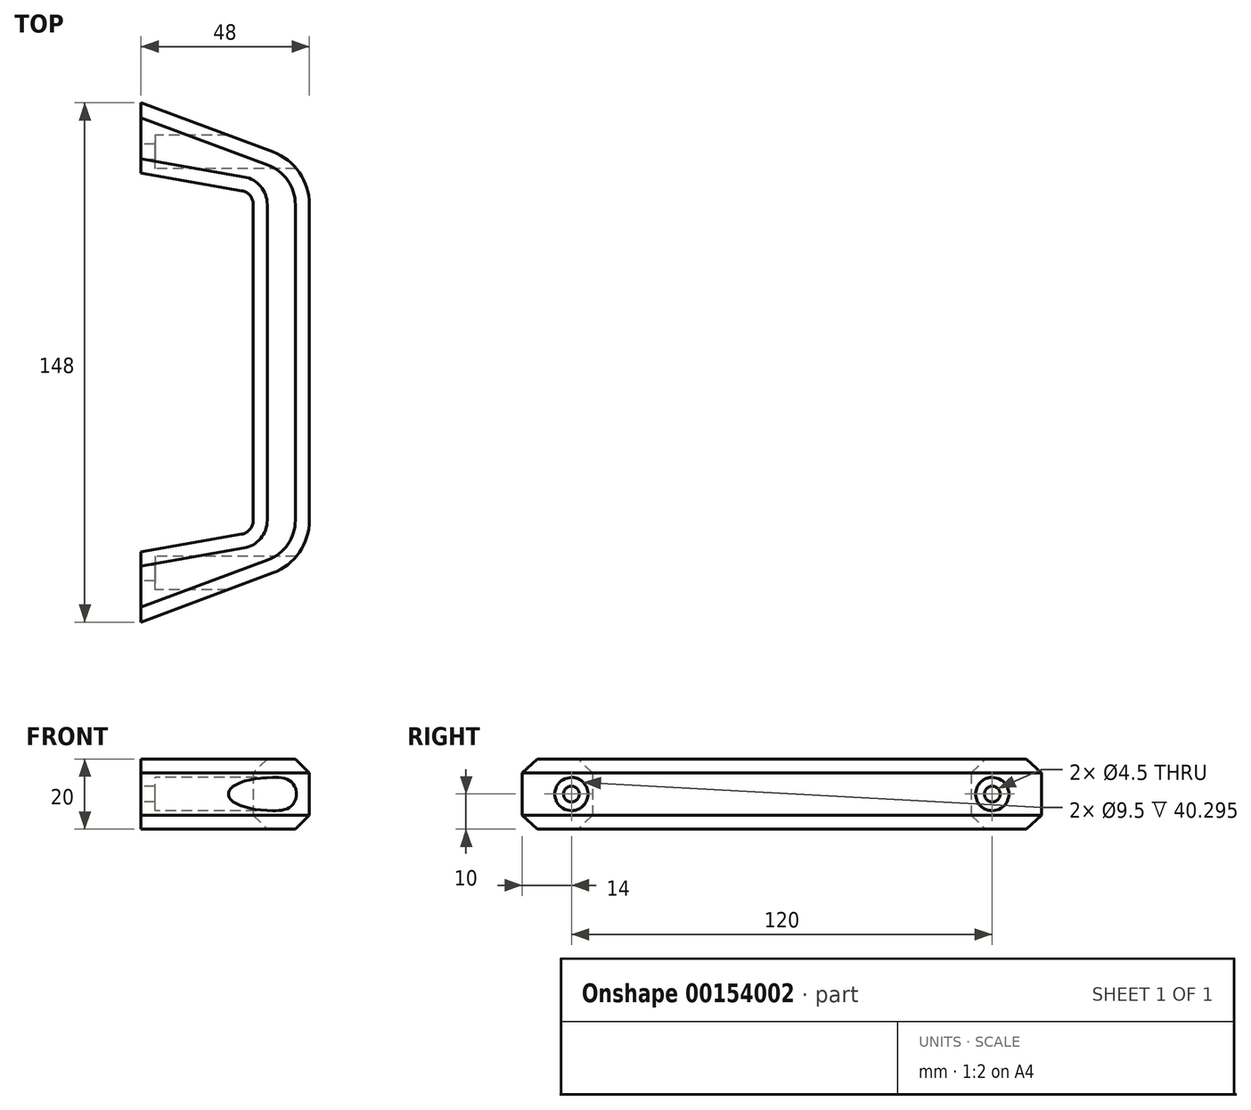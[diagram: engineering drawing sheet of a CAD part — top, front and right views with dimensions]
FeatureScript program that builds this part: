
annotation { "Feature Type Name" : "Feature", "Feature Type Description" : "" }
export const myFeature = defineFeature(function(context is Context, id is Id, definition is map)
    precondition{}
    {
        {
            var Q0;
            Q0=qCreatedBy(makeId("Top.planeOp"),FACE);
            var sketch = newSketch(context, id + "F0", { "sketchPlane" : qUnion([Q0])});
            skLineSegment(sketch, "E0", {"start": v(0, 0) * mm, "end": v(0, -20) * mm});
            skLineSegment(sketch, "E1", {"start": v(0, -128) * mm, "end": v(0, -148) * mm});
            skLineSegment(sketch, "E2", {"start": v(32, -29) * mm, "end": v(32, -119) * mm});
            skLineSegment(sketch, "E3", {"start": v(48, -29) * mm, "end": v(48, -119) * mm});
            skLineSegment(sketch, "E4", {"start": v(0, 0) * mm, "end": v(37.58, -14) * mm});
            skLineSegment(sketch, "E5", {"start": v(0, -148) * mm, "end": v(37.58, -134) * mm});
            skArc(sketch, "E6", {"start": v(48, -29) * mm, "mid": v(45.14, -19.87) * mm, "end": v(37.58, -14) * mm});
            skArc(sketch, "E7", {"start": v(37.58, -134) * mm, "mid": v(45.14, -128.13) * mm, "end": v(48, -119) * mm});
            skLineSegment(sketch, "E8", {"start": v(0, -20) * mm, "end": v(-11.28, -20) * mm, "construction": true});
            skLineSegment(sketch, "E9", {"start": v(0, -128) * mm, "end": v(-20.28, -128) * mm, "construction": true});
            skPoint(sketch, "E10", {"position": v(0, -14) * mm});
            skPoint(sketch, "E11", {"position": v(0, -134) * mm});
            skLineSegment(sketch, "E12", {"start": v(0, -20) * mm, "end": v(28.7, -25.06) * mm});
            skLineSegment(sketch, "E13", {"start": v(0, -128) * mm, "end": v(28.7, -122.94) * mm});
            skArc(sketch, "E14", {"start": v(32, -29) * mm, "mid": v(31.06, -26.43) * mm, "end": v(28.7, -25.06) * mm});
            skArc(sketch, "E15", {"start": v(28.7, -122.94) * mm, "mid": v(31.06, -121.57) * mm, "end": v(32, -119) * mm});
            skSolve(sketch);
        }
        {
            var Q0;
            Q0=makeQuery(id+"F0.imprint","IMPRINT",FACE,{"disambiguationData":[TD([[makeQuery(id+"F0.imprint","IMPRINT",EDGE,{"derivedFrom":sQuery(id+"F0.wireOp",EDGE,"E0")}),1.0]])]});
            extrude(context, id + "F1", {"entities" : qUnion([Q0]), "depth" : 20 * mm});
        }
        {
            var Q0;
            Q0=qCreatedBy(makeId("Right.planeOp"),FACE);
            var sketch = newSketch(context, id + "F2", { "sketchPlane" : qUnion([Q0])});
            skCircle(sketch, "E16", {"center": v(-14, 10) * mm, "radius": 2.25 * mm});
            skCircle(sketch, "E17", {"center": v(-134, 10) * mm, "radius": 2.25 * mm});
            skCircle(sketch, "E18", {"center": v(-14, 10) * mm, "radius": 4.75 * mm});
            skCircle(sketch, "E19", {"center": v(-134, 10) * mm, "radius": 4.75 * mm});
            skSolve(sketch);
        }
        {
            var Q0;
            Q0=makeQuery(id+"F2.imprint","IMPRINT",FACE,{"disambiguationData":[TD([[makeQuery(id+"F2.imprint","IMPRINT",EDGE,{"derivedFrom":sQuery(id+"F2.wireOp",EDGE,"E16")}),1.0]])]});
            var Q1;
            Q1=makeQuery(id+"F2.imprint","IMPRINT",FACE,{"disambiguationData":[TD([[makeQuery(id+"F2.imprint","IMPRINT",EDGE,{"derivedFrom":sQuery(id+"F2.wireOp",EDGE,"E17")}),1.0]])]});
            extrude(context, id + "F3", {"entities" : qUnion([Q0, Q1]), "operationType" : NewBodyOperationType.REMOVE, "endBound" : BoundingType.UP_TO_NEXT, "depth" : 25 * mm});
        }
        {
            var Q0;
            Q0=makeQuery(id+"F2.imprint","IMPRINT",FACE,{"disambiguationData":[TD([[makeQuery(id+"F2.imprint","IMPRINT",EDGE,{"derivedFrom":sQuery(id+"F2.wireOp",EDGE,"E16")}),-1.0]])]});
            var Q1;
            Q1=makeQuery(id+"F2.imprint","IMPRINT",FACE,{"disambiguationData":[TD([[makeQuery(id+"F2.imprint","IMPRINT",EDGE,{"derivedFrom":sQuery(id+"F2.wireOp",EDGE,"E17")}),-1.0]])]});
            extrude(context, id + "F4", {"entities" : qUnion([Q0, Q1]), "operationType" : NewBodyOperationType.REMOVE, "endBound" : BoundingType.UP_TO_NEXT, "depth" : 25 * mm, "hasSecondDirection" : true, "secondDirectionOppositeDirection" : false, "secondDirectionDepth" : 4 * mm});
        }
        {
            var Q0;
            Q0=makeQuery(id+"F1.opExtrude","CAP_EDGE",EDGE,{"disambiguationData":[OSD([sQuery(id+"F0.wireOp",EDGE,"E14")])],"isStart":false});
            var Q1;
            Q1=makeQuery(id+"F1.opExtrude","CAP_EDGE",EDGE,{"disambiguationData":[OSD([sQuery(id+"F0.wireOp",EDGE,"E6")])],"isStart":false});
            var Q2;
            Q2=makeQuery(id+"F1.opExtrude","CAP_EDGE",EDGE,{"disambiguationData":[OSD([sQuery(id+"F0.wireOp",EDGE,"E14")])],"isStart":true});
            var Q3;
            Q3=makeQuery(id+"F1.opExtrude","CAP_EDGE",EDGE,{"disambiguationData":[OSD([sQuery(id+"F0.wireOp",EDGE,"E6")])],"isStart":true});
            chamfer(context, id + "F5", {"entities" : qUnion([Q0, Q1, Q2, Q3]), "width" : 4 * mm, "tangentPropagation" : true});
        }
    });
